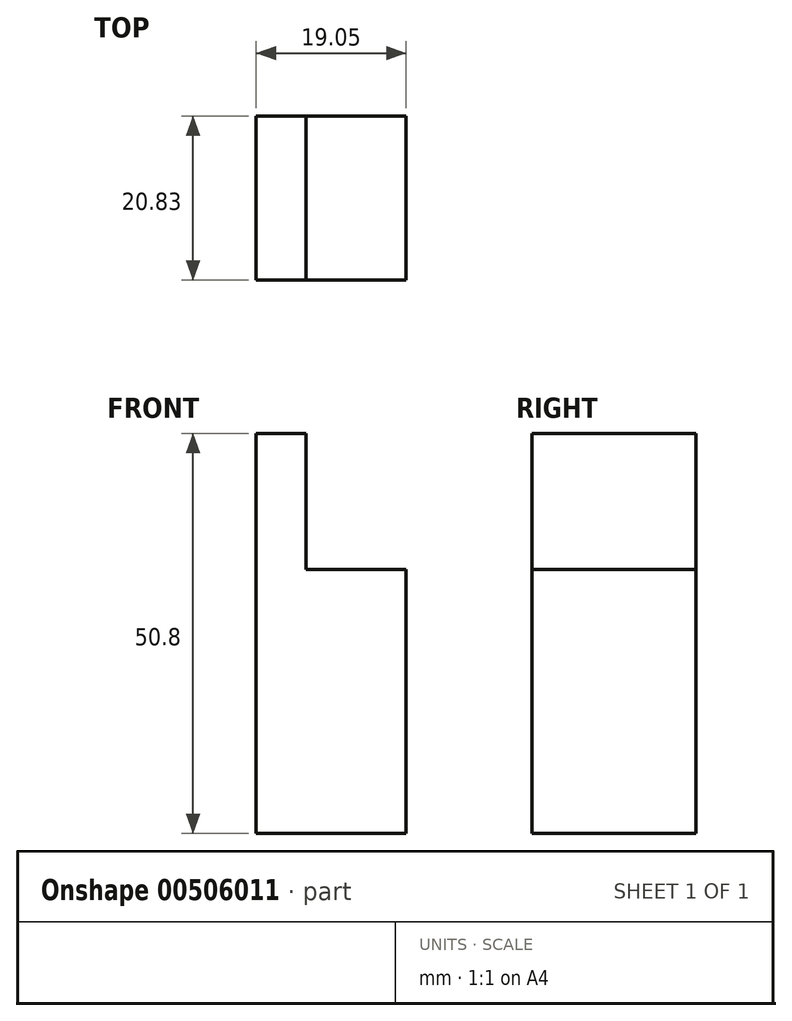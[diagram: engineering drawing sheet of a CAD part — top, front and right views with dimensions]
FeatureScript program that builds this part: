
annotation { "Feature Type Name" : "Feature", "Feature Type Description" : "" }
export const myFeature = defineFeature(function(context is Context, id is Id, definition is map)
    precondition{}
    {
        {
            var Q0;
            Q0=qCreatedBy(makeId("Front.planeOp"),FACE);
            var sketch = newSketch(context, id + "F0", { "sketchPlane" : qUnion([Q0])});
            skLineSegment(sketch, "E0", {"start": v(0, 0) * mm, "end": v(0, 50.8) * mm});
            skLineSegment(sketch, "E1", {"start": v(0, 50.8) * mm, "end": v(6.35, 50.8) * mm});
            skLineSegment(sketch, "E2", {"start": v(6.35, 50.8) * mm, "end": v(6.35, 33.53) * mm});
            skLineSegment(sketch, "E3", {"start": v(6.35, 33.53) * mm, "end": v(19.05, 33.53) * mm});
            skLineSegment(sketch, "E4", {"start": v(19.05, 33.53) * mm, "end": v(19.05, 0) * mm});
            skLineSegment(sketch, "E5", {"start": v(19.05, 0) * mm, "end": v(0, 0) * mm});
            skSolve(sketch);
        }
        {
            var Q0;
            Q0 = qSketchRegion(id + "F0", true);
            extrude(context, id + "F1", {"entities" : qUnion([Q0]), "depth" : 20.83 * mm});
        }
    });
